# Revit family: DoorSpeed XHF AW-DZ для BIM проектирования (REVIT)
name_source: partatom
category: Двери
units: mm (PartAtom-declared; Revit-internal decimal feet)

## family parameters
Всегда вертикально = Да
Общий = Нет
Основа = Стена
При загрузке вырезать с полостями = Нет
Точка расчета площади = Нет

## types (2) — shared parameters
BIMobject category = Industrial Doors
C1 = Да
C2 = Да
C3 = Да
C4 = Да
C5 = Да
Control unit Height = 1500 мм
Date of publishing = 2015-10-01
Depth = 0.00
Design country = Belgium
Edition number = 1
Five Column Windows = Да
Five Row Windows = Да
Four Column Windows = Нет
Four Row Windows = Нет
IFC Classification = Door
Manufacturer country = Belgium
Manufacturer name = Entrematic
Material main = PVC
Material secondary = Steel
NBS Reference Code = 59-23-38
NBS Reference Description = High Speed Doorsets
Nominal height = 550000
Nominal width = 550000
One Column Windows = Нет
One Row Windows = Нет
Option 1 = Stainless steel
Product Guid = a319e3f8-ccd3-4966-8f56-71a75fc3e0bd
Product SKU = dyn-m2-aw
Product data url = https://bimobject.com
Product family = High speed door
Product group = Outside door
QR code = http://bimobject.com
R1 = Да
R2 = Да
R3 = Да
R4 = Да
R5 = Да
Reduced Lintel = Нет
Technical description = https://www.dynacodoor.com
Three Column Windows = Нет
Three Row Windows = Нет
Two Column Windows = Нет
Two Row Windows = Нет
UNSPSC Code = 301715
Uniclass 1.4 Code = L411
Uniclass 1.4 Description = Doors
Uniclass 2.0 Code = PR-59-23-38
Uniclass 2.0 Description = High Speed Doorsets
Unit box = Dynalogic 2 - 380mm x 380mm
Vision Panel Height (400,800) = 400 мм
Аналитическая конструкция = <None>
zero-valued in all types: Weight Net (Kg)

## per-type parameters (varying)
| type | Controle unit Distance | Vision Panel |
| Dynaco_M2_All_Weather_400 | 800 мм | 400 |
| Dynaco_M2_All_Weather_800 | 600 мм | 800 |

## geometry (parser evidence)
native form markers: Blend x14, Sweep x29
no freeform markers — native parametric forms only
